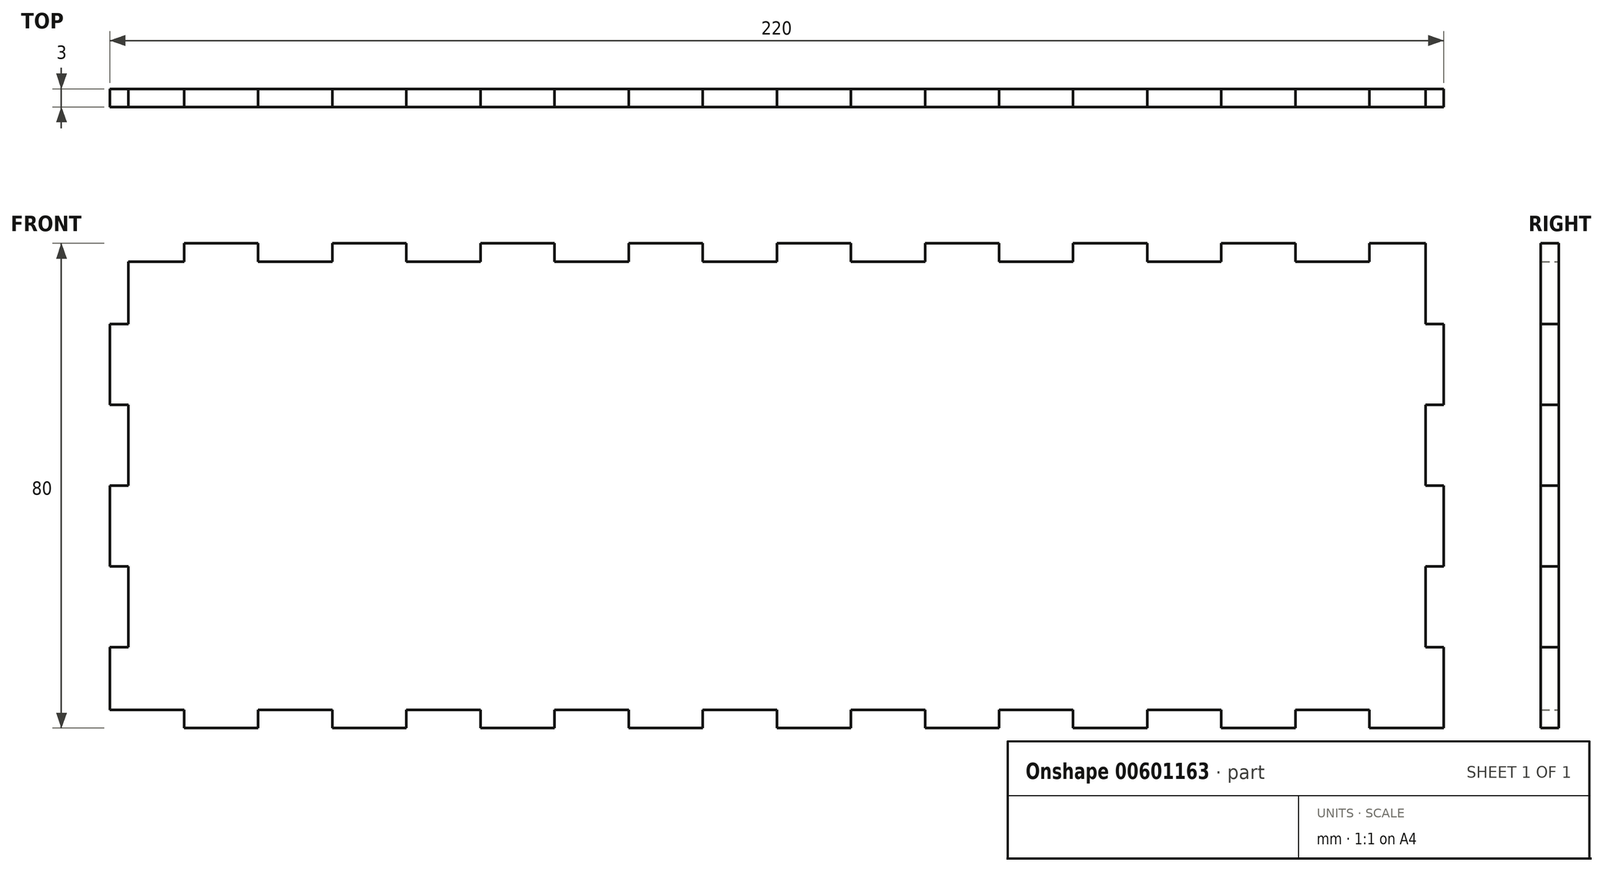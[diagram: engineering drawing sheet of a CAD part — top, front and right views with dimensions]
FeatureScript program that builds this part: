
annotation { "Feature Type Name" : "Feature", "Feature Type Description" : "" }
export const myFeature = defineFeature(function(context is Context, id is Id, definition is map)
    precondition{}
    {
        {
            var Q0;
            Q0=qCreatedBy(makeId("Front.planeOp"),FACE);
            var sketch = newSketch(context, id + "F0", { "sketchPlane" : qUnion([Q0]), "disableImprinting" : false});
            skLineSegment(sketch, "E0.bottom", {"start": v(110, -40) * mm, "end": v(97.78, -40) * mm});
            skLineSegment(sketch, "E0.left", {"start": v(110, -40) * mm, "end": v(110, -26.67) * mm});
            skPoint(sketch, "E0.middle", {"position": v(0, 0) * mm});
            skLineSegment(sketch, "E1", {"start": v(-110, -37) * mm, "end": v(-97.78, -37) * mm});
            skLineSegment(sketch, "E2", {"start": v(-97.78, -37) * mm, "end": v(-97.78, -40) * mm});
            skLineSegment(sketch, "E3", {"start": v(-85.56, -37) * mm, "end": v(-85.56, -40) * mm});
            skLineSegment(sketch, "E4", {"start": v(-73.33, -40) * mm, "end": v(-73.33, -37) * mm});
            skLineSegment(sketch, "E5", {"start": v(-61.11, -37) * mm, "end": v(-61.11, -40) * mm});
            skLineSegment(sketch, "E6", {"start": v(-48.9, -37) * mm, "end": v(-48.9, -40) * mm});
            skLineSegment(sketch, "E7", {"start": v(-36.67, -37) * mm, "end": v(-36.67, -40) * mm});
            skLineSegment(sketch, "E8", {"start": v(-24.45, -40) * mm, "end": v(-24.45, -37) * mm});
            skLineSegment(sketch, "E9", {"start": v(0, -40) * mm, "end": v(0, -37) * mm});
            skLineSegment(sketch, "E10", {"start": v(-12.22, -37) * mm, "end": v(-12.22, -40) * mm});
            skLineSegment(sketch, "E11.MirrorCS", {"start": v(12.22, -37) * mm, "end": v(12.22, -40) * mm});
            skLineSegment(sketch, "E12.MirrorCS", {"start": v(97.78, -37) * mm, "end": v(97.78, -40) * mm});
            skLineSegment(sketch, "E13.MirrorCS", {"start": v(85.56, -37) * mm, "end": v(85.56, -40) * mm});
            skLineSegment(sketch, "E14.MirrorCS", {"start": v(73.33, -40) * mm, "end": v(73.33, -37) * mm});
            skLineSegment(sketch, "E15.MirrorCS", {"start": v(61.11, -37) * mm, "end": v(61.11, -40) * mm});
            skLineSegment(sketch, "E16.MirrorCS", {"start": v(48.9, -37) * mm, "end": v(48.9, -40) * mm});
            skLineSegment(sketch, "E17.MirrorCS", {"start": v(36.67, -37) * mm, "end": v(36.67, -40) * mm});
            skLineSegment(sketch, "E18.MirrorCS", {"start": v(24.45, -40) * mm, "end": v(24.45, -37) * mm});
            skPoint(sketch, "E19.orphan", {"position": v(-110, -40) * mm});
            skLineSegment(sketch, "E20.trimOffspring", {"start": v(-85.56, -37) * mm, "end": v(-73.33, -37) * mm});
            skLineSegment(sketch, "E21.trimOffspring", {"start": v(-85.56, -40) * mm, "end": v(-97.78, -40) * mm});
            skLineSegment(sketch, "E22.trimOffspring", {"start": v(-61.11, -37) * mm, "end": v(-48.9, -37) * mm});
            skLineSegment(sketch, "E23.trimOffspring", {"start": v(-61.11, -40) * mm, "end": v(-73.33, -40) * mm});
            skLineSegment(sketch, "E24.trimOffspring", {"start": v(-36.67, -37) * mm, "end": v(-24.45, -37) * mm});
            skLineSegment(sketch, "E25.trimOffspring", {"start": v(-36.67, -40) * mm, "end": v(-48.9, -40) * mm});
            skLineSegment(sketch, "E26.trimOffspring", {"start": v(-12.22, -37) * mm, "end": v(0, -37) * mm});
            skLineSegment(sketch, "E27.trimOffspring", {"start": v(-12.22, -40) * mm, "end": v(-24.45, -40) * mm});
            skLineSegment(sketch, "E28.trimOffspring", {"start": v(12.22, -37) * mm, "end": v(24.45, -37) * mm});
            skLineSegment(sketch, "E29.trimOffspring", {"start": v(12.22, -40) * mm, "end": v(0, -40) * mm});
            skLineSegment(sketch, "E30.trimOffspring", {"start": v(36.67, -37) * mm, "end": v(48.9, -37) * mm});
            skLineSegment(sketch, "E31.trimOffspring", {"start": v(36.67, -40) * mm, "end": v(24.45, -40) * mm});
            skLineSegment(sketch, "E32.trimOffspring", {"start": v(61.11, -37) * mm, "end": v(73.33, -37) * mm});
            skLineSegment(sketch, "E33.trimOffspring", {"start": v(61.11, -40) * mm, "end": v(48.9, -40) * mm});
            skLineSegment(sketch, "E34.trimOffspring", {"start": v(85.56, -37) * mm, "end": v(97.78, -37) * mm});
            skLineSegment(sketch, "E35.trimOffspring", {"start": v(85.56, -40) * mm, "end": v(73.33, -40) * mm});
            skLineSegment(sketch, "E36.MirrorCS", {"start": v(0, 40) * mm, "end": v(0, 37) * mm});
            skLineSegment(sketch, "E37.MirrorCS", {"start": v(48.9, 37) * mm, "end": v(48.9, 40) * mm});
            skLineSegment(sketch, "E38.MirrorCS", {"start": v(97.78, 37) * mm, "end": v(97.78, 40) * mm});
            skLineSegment(sketch, "E39.MirrorCS", {"start": v(85.56, 37) * mm, "end": v(85.56, 40) * mm});
            skLineSegment(sketch, "E40.MirrorCS", {"start": v(73.33, 40) * mm, "end": v(73.33, 37) * mm});
            skLineSegment(sketch, "E41.MirrorCS", {"start": v(36.67, 37) * mm, "end": v(36.67, 40) * mm});
            skLineSegment(sketch, "E42.MirrorCS", {"start": v(24.45, 40) * mm, "end": v(24.45, 37) * mm});
            skLineSegment(sketch, "E43.MirrorCS", {"start": v(12.22, 37) * mm, "end": v(12.22, 40) * mm});
            skLineSegment(sketch, "E44.MirrorCS", {"start": v(-12.22, 37) * mm, "end": v(-12.22, 40) * mm});
            skLineSegment(sketch, "E45.MirrorCS", {"start": v(-24.45, 40) * mm, "end": v(-24.45, 37) * mm});
            skLineSegment(sketch, "E46.MirrorCS", {"start": v(-36.67, 37) * mm, "end": v(-36.67, 40) * mm});
            skLineSegment(sketch, "E47.MirrorCS", {"start": v(-48.9, 37) * mm, "end": v(-48.9, 40) * mm});
            skLineSegment(sketch, "E48.MirrorCS", {"start": v(-61.11, 37) * mm, "end": v(-61.11, 40) * mm});
            skLineSegment(sketch, "E49.MirrorCS", {"start": v(-73.33, 40) * mm, "end": v(-73.33, 37) * mm});
            skLineSegment(sketch, "E50.MirrorCS", {"start": v(-85.56, 37) * mm, "end": v(-85.56, 40) * mm});
            skLineSegment(sketch, "E51.MirrorCS", {"start": v(-97.78, 37) * mm, "end": v(-97.78, 40) * mm});
            skLineSegment(sketch, "E52.MirrorCS", {"start": v(61.11, 37) * mm, "end": v(61.11, 40) * mm});
            skLineSegment(sketch, "E53.MirrorCS", {"start": v(-36.67, 37) * mm, "end": v(-24.45, 37) * mm});
            skLineSegment(sketch, "E54.MirrorCS", {"start": v(61.11, 37) * mm, "end": v(73.33, 37) * mm});
            skLineSegment(sketch, "E55.MirrorCS", {"start": v(12.22, 40) * mm, "end": v(0, 40) * mm});
            skLineSegment(sketch, "E56.MirrorCS", {"start": v(-85.56, 37) * mm, "end": v(-73.33, 37) * mm});
            skLineSegment(sketch, "E57.MirrorCS", {"start": v(107, 40) * mm, "end": v(97.78, 40) * mm});
            skLineSegment(sketch, "E58.MirrorCS", {"start": v(85.56, 40) * mm, "end": v(73.33, 40) * mm});
            skLineSegment(sketch, "E59.MirrorCS", {"start": v(36.67, 40) * mm, "end": v(24.45, 40) * mm});
            skLineSegment(sketch, "E60.MirrorCS", {"start": v(12.22, 37) * mm, "end": v(24.45, 37) * mm});
            skLineSegment(sketch, "E61.MirrorCS", {"start": v(-61.11, 37) * mm, "end": v(-48.9, 37) * mm});
            skLineSegment(sketch, "E62.MirrorCS", {"start": v(-12.22, 37) * mm, "end": v(0, 37) * mm});
            skLineSegment(sketch, "E63.MirrorCS", {"start": v(36.67, 37) * mm, "end": v(48.9, 37) * mm});
            skLineSegment(sketch, "E64.MirrorCS", {"start": v(-61.11, 40) * mm, "end": v(-73.33, 40) * mm});
            skLineSegment(sketch, "E65.MirrorCS", {"start": v(85.56, 37) * mm, "end": v(97.78, 37) * mm});
            skLineSegment(sketch, "E66.MirrorCS", {"start": v(-12.22, 40) * mm, "end": v(-24.45, 40) * mm});
            skLineSegment(sketch, "E67.MirrorCS", {"start": v(61.11, 40) * mm, "end": v(48.9, 40) * mm});
            skLineSegment(sketch, "E68.MirrorCS", {"start": v(-85.56, 40) * mm, "end": v(-97.78, 40) * mm});
            skLineSegment(sketch, "E69.MirrorCS", {"start": v(-36.67, 40) * mm, "end": v(-48.9, 40) * mm});
            skLineSegment(sketch, "E70.MirrorCS", {"start": v(-107, 37) * mm, "end": v(-97.78, 37) * mm});
            skPoint(sketch, "E71.MirrorP", {"position": v(-110, 40) * mm});
            skLineSegment(sketch, "E72", {"start": v(107, 40) * mm, "end": v(107, 26.67) * mm});
            skLineSegment(sketch, "E73", {"start": v(107, 26.67) * mm, "end": v(110, 26.67) * mm});
            skLineSegment(sketch, "E74", {"start": v(107, 13.33) * mm, "end": v(110, 13.33) * mm});
            skLineSegment(sketch, "E75", {"start": v(107, 0) * mm, "end": v(110, 0) * mm});
            skLineSegment(sketch, "E76.MirrorCS", {"start": v(107, -26.67) * mm, "end": v(110, -26.67) * mm});
            skLineSegment(sketch, "E77.MirrorCS", {"start": v(107, -13.33) * mm, "end": v(110, -13.33) * mm});
            skPoint(sketch, "E78.orphan", {"position": v(110, 40) * mm});
            skLineSegment(sketch, "E79.trimOffspring", {"start": v(107, 13.33) * mm, "end": v(107, 0) * mm});
            skLineSegment(sketch, "E80.trimOffspring", {"start": v(110, 13.33) * mm, "end": v(110, 26.67) * mm});
            skLineSegment(sketch, "E81.trimOffspring", {"start": v(107, -13.33) * mm, "end": v(107, -26.67) * mm});
            skLineSegment(sketch, "E82.trimOffspring", {"start": v(110, -13.33) * mm, "end": v(110, 0) * mm});
            skLineSegment(sketch, "E83.MirrorCS", {"start": v(-107, 0) * mm, "end": v(-110, 0) * mm});
            skLineSegment(sketch, "E84.MirrorCS", {"start": v(-107, 26.67) * mm, "end": v(-110, 26.67) * mm});
            skLineSegment(sketch, "E85.MirrorCS", {"start": v(-107, 13.33) * mm, "end": v(-110, 13.33) * mm});
            skLineSegment(sketch, "E86.MirrorCS", {"start": v(-107, -26.67) * mm, "end": v(-110, -26.67) * mm});
            skLineSegment(sketch, "E87.MirrorCS", {"start": v(-107, -13.33) * mm, "end": v(-110, -13.33) * mm});
            skLineSegment(sketch, "E88.MirrorCS", {"start": v(-110, -13.33) * mm, "end": v(-110, 0) * mm});
            skLineSegment(sketch, "E89.MirrorCS", {"start": v(-107, 37) * mm, "end": v(-107, 26.67) * mm});
            skLineSegment(sketch, "E90.MirrorCS", {"start": v(-107, -13.33) * mm, "end": v(-107, -26.67) * mm});
            skLineSegment(sketch, "E91.MirrorCS", {"start": v(-110, 13.33) * mm, "end": v(-110, 26.67) * mm});
            skLineSegment(sketch, "E92.MirrorCS", {"start": v(-110, -37) * mm, "end": v(-110, -26.67) * mm});
            skLineSegment(sketch, "E93.MirrorCS", {"start": v(-107, 13.33) * mm, "end": v(-107, 0) * mm});
            skPoint(sketch, "E94.orphan", {"position": v(-107, 40) * mm});
            skPoint(sketch, "E95.orphan", {"position": v(-110, 37) * mm});
            skSolve(sketch);
        }
        {
            var Q0;
            Q0=makeQuery(id+"F0.imprint","IMPRINT",FACE,{"disambiguationData":[TD([[makeQuery(id+"F0.imprint","IMPRINT",EDGE,{"derivedFrom":sQuery(id+"F0.wireOp",EDGE,"E0.bottom")}),-1.0]])]});
            extrude(context, id + "F1", {"entities" : qUnion([Q0]), "depth" : 3 * mm, "offsetDistance" : 25 * mm});
        }
    });
